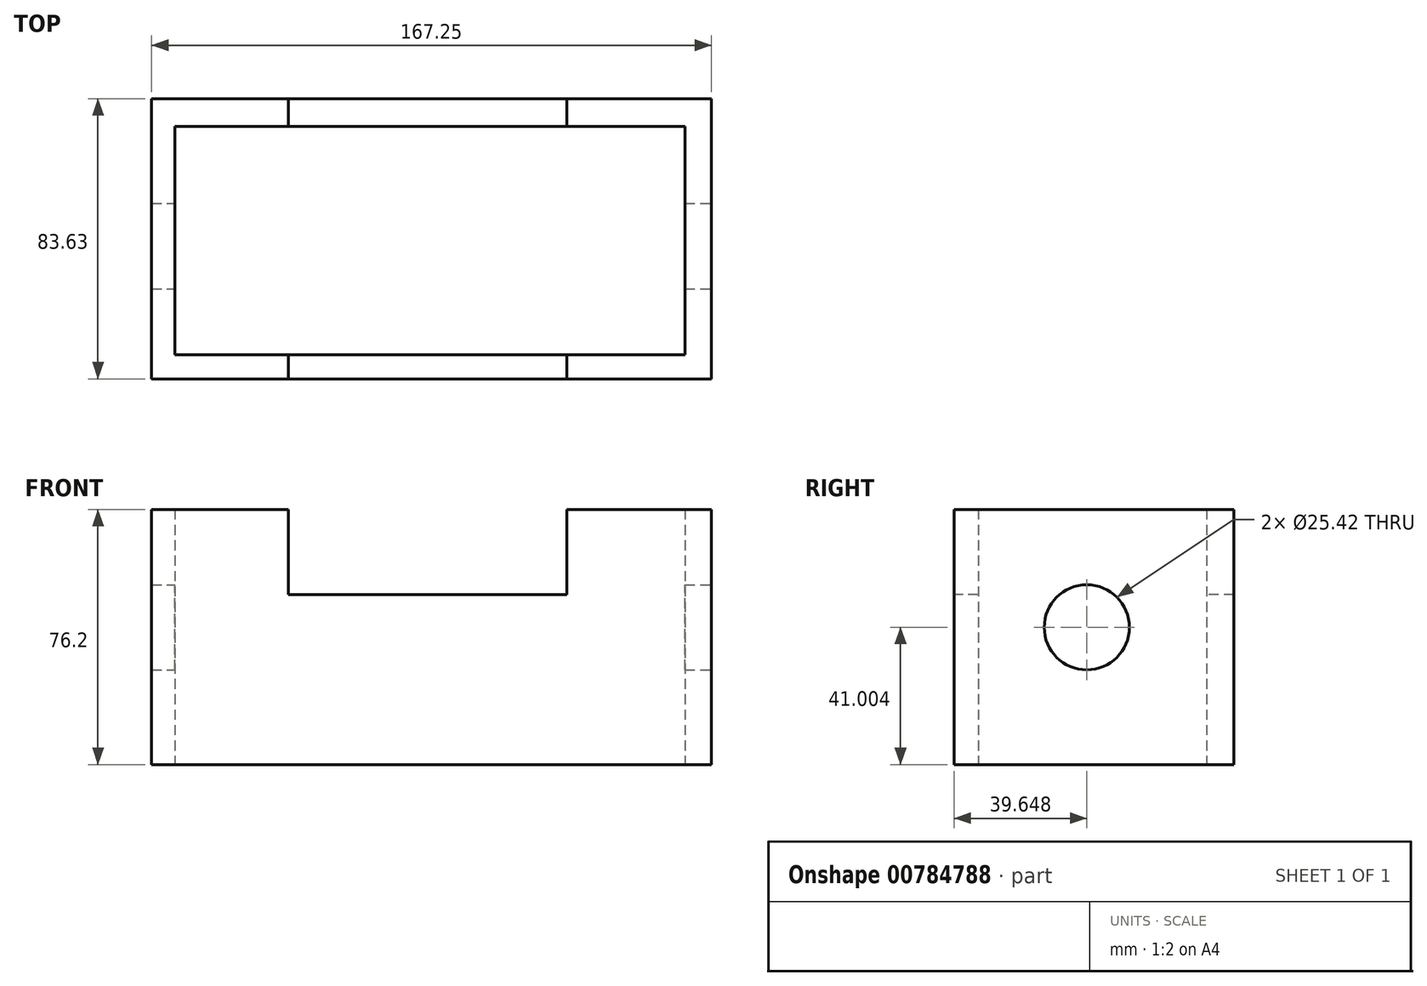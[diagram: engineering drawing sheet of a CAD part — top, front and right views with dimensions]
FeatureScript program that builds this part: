
annotation { "Feature Type Name" : "Feature", "Feature Type Description" : "" }
export const myFeature = defineFeature(function(context is Context, id is Id, definition is map)
    precondition{}
    {
        {
            var Q0;
            Q0=qCreatedBy(makeId("Top.planeOp"),FACE);
            var sketch = newSketch(context, id + "F0", { "sketchPlane" : qUnion([Q0])});
            skLineSegment(sketch, "E0.bottom", {"start": v(-76.27, 36.75) * mm, "end": v(76.03, 36.75) * mm});
            skLineSegment(sketch, "E0.top", {"start": v(-76.27, -31.45) * mm, "end": v(76.03, -31.45) * mm});
            skLineSegment(sketch, "E0.left", {"start": v(-76.27, 36.75) * mm, "end": v(-76.27, -31.45) * mm});
            skLineSegment(sketch, "E0.right", {"start": v(76.03, 36.75) * mm, "end": v(76.03, -31.45) * mm});
            skLineSegment(sketch, "E1.bottom", {"start": v(-83.26, 44.95) * mm, "end": v(83.99, 44.95) * mm});
            skLineSegment(sketch, "E1.top", {"start": v(-83.26, -38.68) * mm, "end": v(83.99, -38.68) * mm});
            skLineSegment(sketch, "E1.left", {"start": v(-83.26, 44.95) * mm, "end": v(-83.26, -38.68) * mm});
            skLineSegment(sketch, "E1.right", {"start": v(83.99, 44.95) * mm, "end": v(83.99, -38.68) * mm});
            skSolve(sketch);
        }
        {
            var Q0;
            Q0=makeQuery(id+"F0.imprint","IMPRINT",FACE,{"disambiguationData":[TD([[makeQuery(id+"F0.imprint","IMPRINT",EDGE,{"derivedFrom":sQuery(id+"F0.wireOp",EDGE,"E0.bottom")}),1.0]])]});
            extrude(context, id + "F1", {"entities" : qUnion([Q0]), "depth" : 50.8 * mm, "offsetDistance" : 25.4 * mm});
        }
        {
            var Q0;
            Q0=makeQuery(id+"F1.opExtrude","CAP_FACE",FACE,{"disambiguationData":[OSD([sQuery(id+"F0.wireOp",EDGE,"E0.bottom"),sQuery(id+"F0.wireOp",EDGE,"E0.top"),sQuery(id+"F0.wireOp",EDGE,"E0.left"),sQuery(id+"F0.wireOp",EDGE,"E0.right"),sQuery(id+"F0.wireOp",EDGE,"E1.bottom"),sQuery(id+"F0.wireOp",EDGE,"E1.top"),sQuery(id+"F0.wireOp",EDGE,"E1.left"),sQuery(id+"F0.wireOp",EDGE,"E1.right")])],"isStart":false});
            var sketch = newSketch(context, id + "F2", { "sketchPlane" : qUnion([Q0])});
            skLineSegment(sketch, "E2", {"start": v(-42.41, 44.95) * mm, "end": v(-42.41, 36.75) * mm});
            skLineSegment(sketch, "E3", {"start": v(-42.41, -31.45) * mm, "end": v(-42.41, -38.68) * mm});
            skLineSegment(sketch, "E4", {"start": v(40.73, 44.95) * mm, "end": v(40.73, 36.75) * mm});
            skLineSegment(sketch, "E5", {"start": v(40.73, -31.45) * mm, "end": v(40.73, -38.68) * mm});
            skSolve(sketch);
        }
        {
            var Q0;
            {var subQ4=sQuery(id+"F2.wireOp",EDGE,"E2");Q0=makeQuery(id+"F2.imprint","IMPRINT",FACE,{"disambiguationData":[TD([[makeQuery(id+"F2.imprint","IMPRINT",EDGE,{"derivedFrom":subQ4}),-1.0]])]});}
            var Q1;
            {var subQ4=sQuery(id+"F2.wireOp",EDGE,"E4");Q1=makeQuery(id+"F2.imprint","IMPRINT",FACE,{"disambiguationData":[TD([[makeQuery(id+"F2.imprint","IMPRINT",EDGE,{"derivedFrom":subQ4}),1.0]])]});}
            extrude(context, id + "F3", {"entities" : qUnion([Q0, Q1]), "operationType" : NewBodyOperationType.ADD, "depth" : 25.4 * mm, "offsetDistance" : 25.4 * mm});
        }
        {
            var Q0;
            {var subQ0=sQuery(id+"F0.wireOp",EDGE,"E1.right");Q0=makeQuery(id+"F3.boolean.opBoolean","MERGE",FACE,{"derivedFrom":[makeQuery(id+"F1.opExtrude","SWEPT_FACE",FACE,{"disambiguationData":[OSD([subQ0])]}),makeQuery(id+"F3.opExtrude","SWEPT_FACE",FACE,{"disambiguationData":[OSD([subQ0])]})]});}
            var sketch = newSketch(context, id + "F4", { "sketchPlane" : qUnion([Q0])});
            skCircle(sketch, "E6", {"center": v(0.97, 41) * mm, "radius": 12.71 * mm});
            skSolve(sketch);
        }
        {
            var Q0;
            Q0=makeQuery(id+"F4.imprint","IMPRINT",FACE,{"disambiguationData":[TD([[makeQuery(id+"F4.imprint","IMPRINT",EDGE,{"derivedFrom":sQuery(id+"F4.wireOp",EDGE,"E6")}),1.0]])]});
            extrude(context, id + "F5", {"entities" : qUnion([Q0]), "operationType" : NewBodyOperationType.REMOVE, "oppositeDirection" : true, "depth" : 226.06 * mm, "offsetDistance" : 25.4 * mm});
        }
    });
